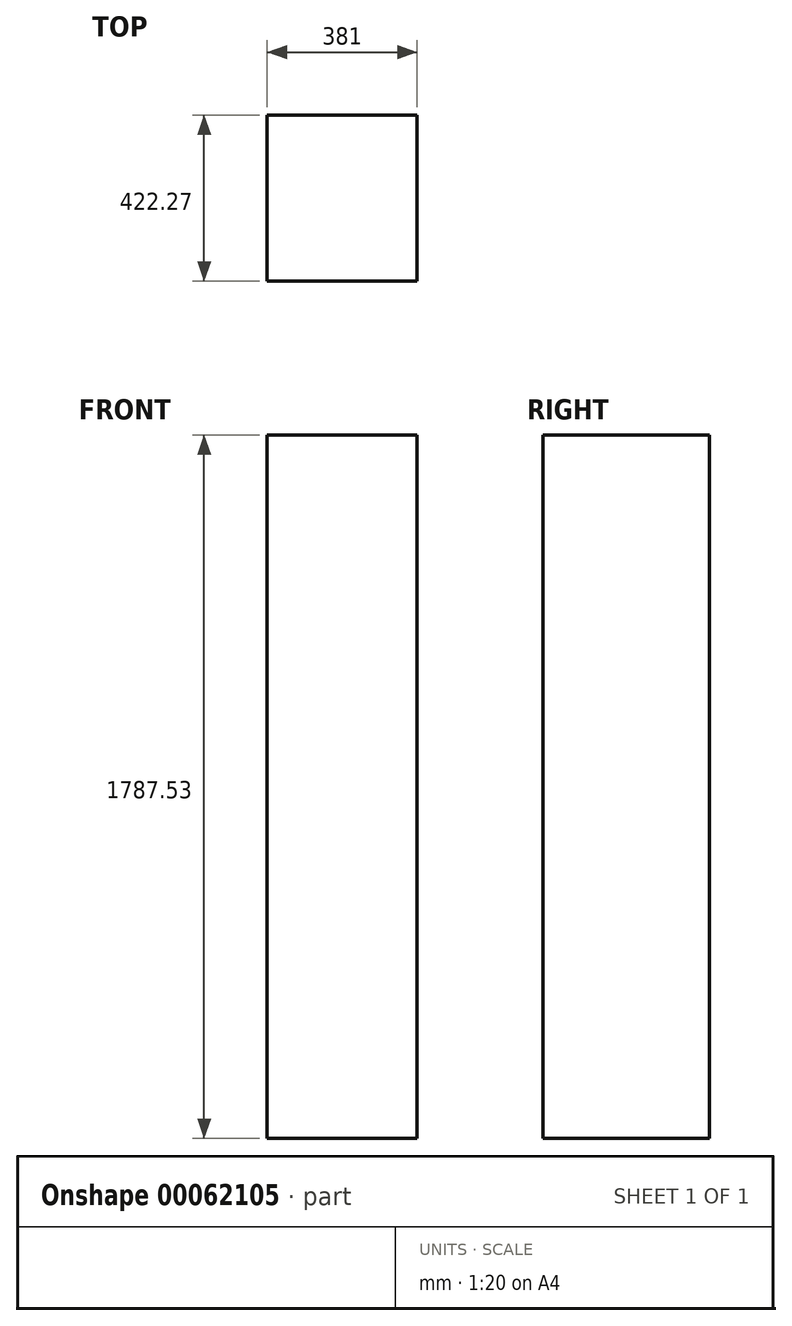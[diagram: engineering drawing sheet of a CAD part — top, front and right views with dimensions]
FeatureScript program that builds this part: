
annotation { "Feature Type Name" : "Feature", "Feature Type Description" : "" }
export const myFeature = defineFeature(function(context is Context, id is Id, definition is map)
    precondition{}
    {
        {
            var Q0;
            Q0=qCreatedBy(makeId("Top.planeOp"),FACE);
            var sketch = newSketch(context, id + "F0", { "sketchPlane" : qUnion([Q0])});
            skLineSegment(sketch, "E0.bottom", {"start": v(-186.35, 293.84) * mm, "end": v(194.65, 293.84) * mm});
            skLineSegment(sketch, "E0.top", {"start": v(-186.35, -128.43) * mm, "end": v(194.65, -128.43) * mm});
            skLineSegment(sketch, "E0.left", {"start": v(-186.35, 293.84) * mm, "end": v(-186.35, -128.43) * mm});
            skLineSegment(sketch, "E0.right", {"start": v(194.65, 293.84) * mm, "end": v(194.65, -128.43) * mm});
            skSolve(sketch);
        }
        {
            var Q0;
            Q0=makeQuery(id+"F0.imprint","IMPRINT",FACE,{"disambiguationData":[TD([[makeQuery(id+"F0.imprint","IMPRINT",EDGE,{"derivedFrom":sQuery(id+"F0.wireOp",EDGE,"E0.bottom")}),-1.0]])]});
            extrude(context, id + "F1", {"entities" : qUnion([Q0]), "depth" : 1787.52 * mm});
        }
    });
